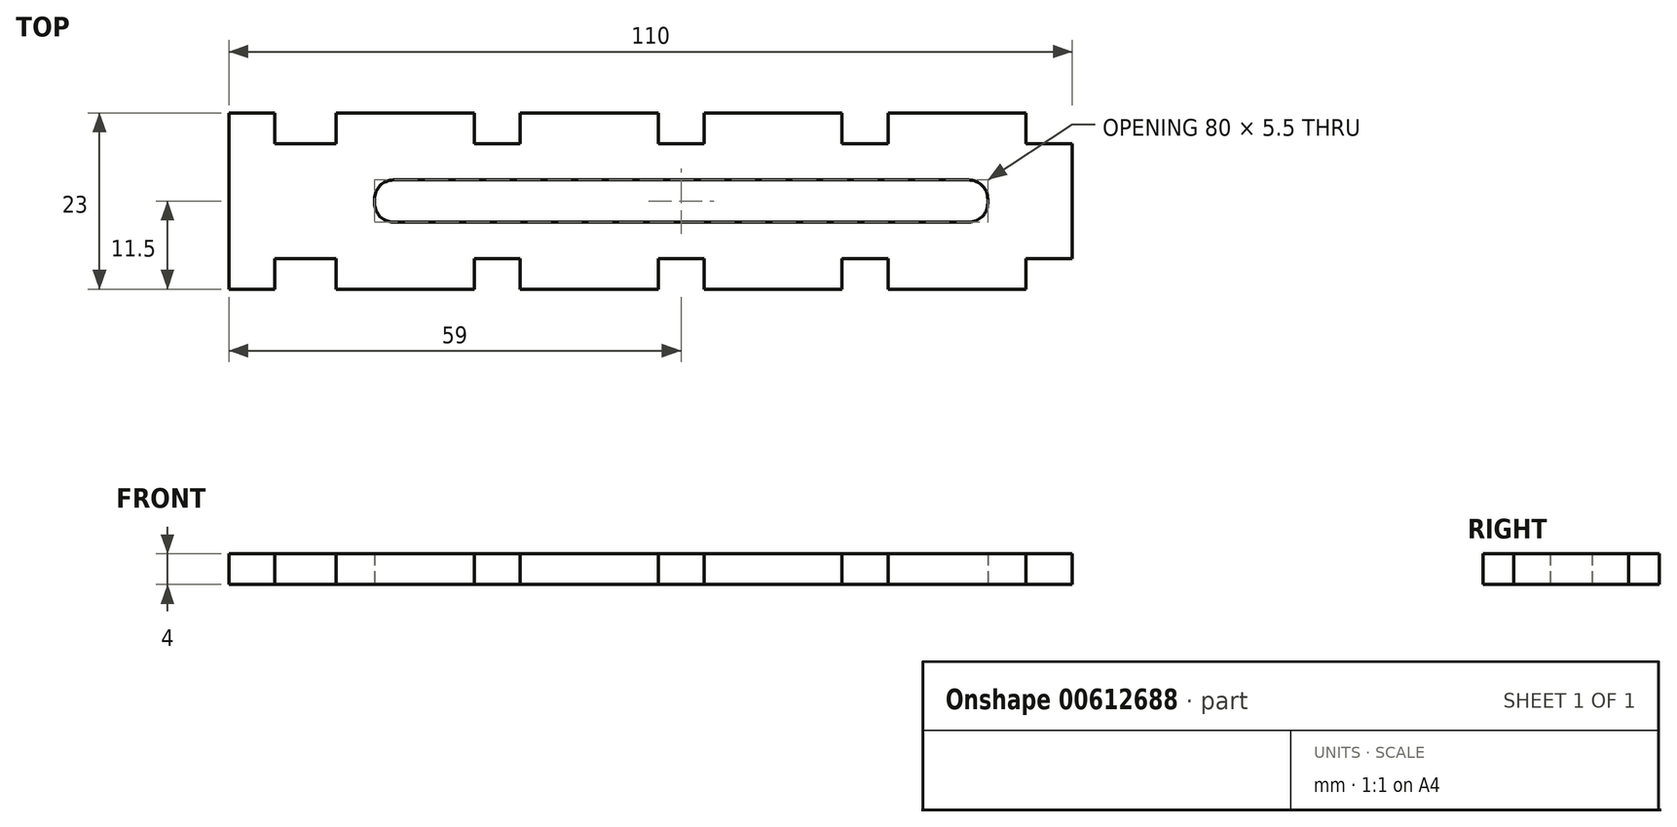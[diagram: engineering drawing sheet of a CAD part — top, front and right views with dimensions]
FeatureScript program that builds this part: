
annotation { "Feature Type Name" : "Feature", "Feature Type Description" : "" }
export const myFeature = defineFeature(function(context is Context, id is Id, definition is map)
    precondition{}
    {
        {
            var Q0;
            Q0=qCreatedBy(makeId("Top.planeOp"),FACE);
            var sketch = newSketch(context, id + "F0", { "sketchPlane" : qUnion([Q0])});
            skLineSegment(sketch, "E0", {"start": v(-55, -11.5) * mm, "end": v(-55, 11.5) * mm});
            skLineSegment(sketch, "E1", {"start": v(-49, 7.5) * mm, "end": v(-49, 11.5) * mm});
            skLineSegment(sketch, "E2", {"start": v(-49, -11.5) * mm, "end": v(-49, -7.5) * mm});
            skLineSegment(sketch, "E3", {"start": v(-41, 7.5) * mm, "end": v(-41, 11.5) * mm});
            skLineSegment(sketch, "E4", {"start": v(-41, -11.5) * mm, "end": v(-41, -7.5) * mm});
            skLineSegment(sketch, "E5", {"start": v(-23, 7.5) * mm, "end": v(-23, 11.5) * mm});
            skLineSegment(sketch, "E6", {"start": v(-23, -11.5) * mm, "end": v(-23, -7.5) * mm});
            skLineSegment(sketch, "E7", {"start": v(-17, 7.5) * mm, "end": v(-17, 11.5) * mm});
            skLineSegment(sketch, "E8", {"start": v(-17, -11.5) * mm, "end": v(-17, -7.5) * mm});
            skLineSegment(sketch, "E9", {"start": v(1, 7.5) * mm, "end": v(1, 11.5) * mm});
            skLineSegment(sketch, "E10", {"start": v(1, -11.5) * mm, "end": v(1, -7.5) * mm});
            skLineSegment(sketch, "E11", {"start": v(7, 7.5) * mm, "end": v(7, 11.5) * mm});
            skLineSegment(sketch, "E12", {"start": v(7, -11.5) * mm, "end": v(7, -7.5) * mm});
            skLineSegment(sketch, "E13", {"start": v(25, 7.5) * mm, "end": v(25, 11.5) * mm});
            skLineSegment(sketch, "E14", {"start": v(25, -11.5) * mm, "end": v(25, -7.5) * mm});
            skLineSegment(sketch, "E15", {"start": v(31, 7.5) * mm, "end": v(31, 11.5) * mm});
            skLineSegment(sketch, "E16", {"start": v(31, -11.5) * mm, "end": v(31, -7.5) * mm});
            skLineSegment(sketch, "E17", {"start": v(49, 7.5) * mm, "end": v(49, 11.5) * mm});
            skLineSegment(sketch, "E18", {"start": v(49, -11.5) * mm, "end": v(49, -7.5) * mm});
            skLineSegment(sketch, "E19", {"start": v(55, -7.5) * mm, "end": v(55, 7.5) * mm});
            skLineSegment(sketch, "E20", {"start": v(49, -11.5) * mm, "end": v(31, -11.5) * mm});
            skLineSegment(sketch, "E21", {"start": v(25, -11.5) * mm, "end": v(7, -11.5) * mm});
            skLineSegment(sketch, "E22", {"start": v(1, -11.5) * mm, "end": v(-17, -11.5) * mm});
            skLineSegment(sketch, "E23", {"start": v(-23, -11.5) * mm, "end": v(-41, -11.5) * mm});
            skLineSegment(sketch, "E24", {"start": v(-49, -11.5) * mm, "end": v(-55, -11.5) * mm});
            skLineSegment(sketch, "E25", {"start": v(31, -7.5) * mm, "end": v(25, -7.5) * mm});
            skLineSegment(sketch, "E26", {"start": v(55, -7.5) * mm, "end": v(49, -7.5) * mm});
            skLineSegment(sketch, "E27", {"start": v(7, -7.5) * mm, "end": v(1, -7.5) * mm});
            skLineSegment(sketch, "E28", {"start": v(-17, -7.5) * mm, "end": v(-23, -7.5) * mm});
            skLineSegment(sketch, "E29", {"start": v(-41, -7.5) * mm, "end": v(-49, -7.5) * mm});
            skLineSegment(sketch, "E30", {"start": v(31, 7.5) * mm, "end": v(25, 7.5) * mm});
            skLineSegment(sketch, "E31", {"start": v(55, 7.5) * mm, "end": v(49, 7.5) * mm});
            skLineSegment(sketch, "E32", {"start": v(7, 7.5) * mm, "end": v(1, 7.5) * mm});
            skLineSegment(sketch, "E33", {"start": v(-17, 7.5) * mm, "end": v(-23, 7.5) * mm});
            skLineSegment(sketch, "E34", {"start": v(-41, 7.5) * mm, "end": v(-49, 7.5) * mm});
            skLineSegment(sketch, "E35", {"start": v(49, 11.5) * mm, "end": v(31, 11.5) * mm});
            skLineSegment(sketch, "E36", {"start": v(25, 11.5) * mm, "end": v(7, 11.5) * mm});
            skLineSegment(sketch, "E37", {"start": v(1, 11.5) * mm, "end": v(-17, 11.5) * mm});
            skLineSegment(sketch, "E38", {"start": v(-23, 11.5) * mm, "end": v(-41, 11.5) * mm});
            skLineSegment(sketch, "E39", {"start": v(-49, 11.5) * mm, "end": v(-55, 11.5) * mm});
            skArc(sketch, "E40", {"start": v(-33.5, 2.75) * mm, "mid": v(-35.27, 2.02) * mm, "end": v(-36, 0.25) * mm});
            skLineSegment(sketch, "E41", {"start": v(-36, 0.25) * mm, "end": v(-36, -0.25) * mm});
            skArc(sketch, "E42", {"start": v(-36, -0.25) * mm, "mid": v(-35.27, -2.02) * mm, "end": v(-33.5, -2.75) * mm});
            skLineSegment(sketch, "E43", {"start": v(-33.5, -2.75) * mm, "end": v(41.5, -2.75) * mm});
            skArc(sketch, "E44", {"start": v(41.5, -2.75) * mm, "mid": v(43.27, -2.02) * mm, "end": v(44, -0.25) * mm});
            skLineSegment(sketch, "E45", {"start": v(44, -0.25) * mm, "end": v(44, 0.25) * mm});
            skArc(sketch, "E46", {"start": v(44, 0.25) * mm, "mid": v(43.27, 2.02) * mm, "end": v(41.5, 2.75) * mm});
            skLineSegment(sketch, "E47", {"start": v(41.5, 2.75) * mm, "end": v(-33.5, 2.75) * mm});
            skSolve(sketch);
        }
        {
            var Q0;
            Q0=makeQuery(id+"F0.imprint","IMPRINT",FACE,{"disambiguationData":[TD([[makeQuery(id+"F0.imprint","IMPRINT",EDGE,{"derivedFrom":sQuery(id+"F0.wireOp",EDGE,"E0")}),-1.0]])]});
            extrude(context, id + "F1", {"entities" : qUnion([Q0]), "depth" : 4 * mm, "offsetDistance" : 25 * mm});
        }
    });
